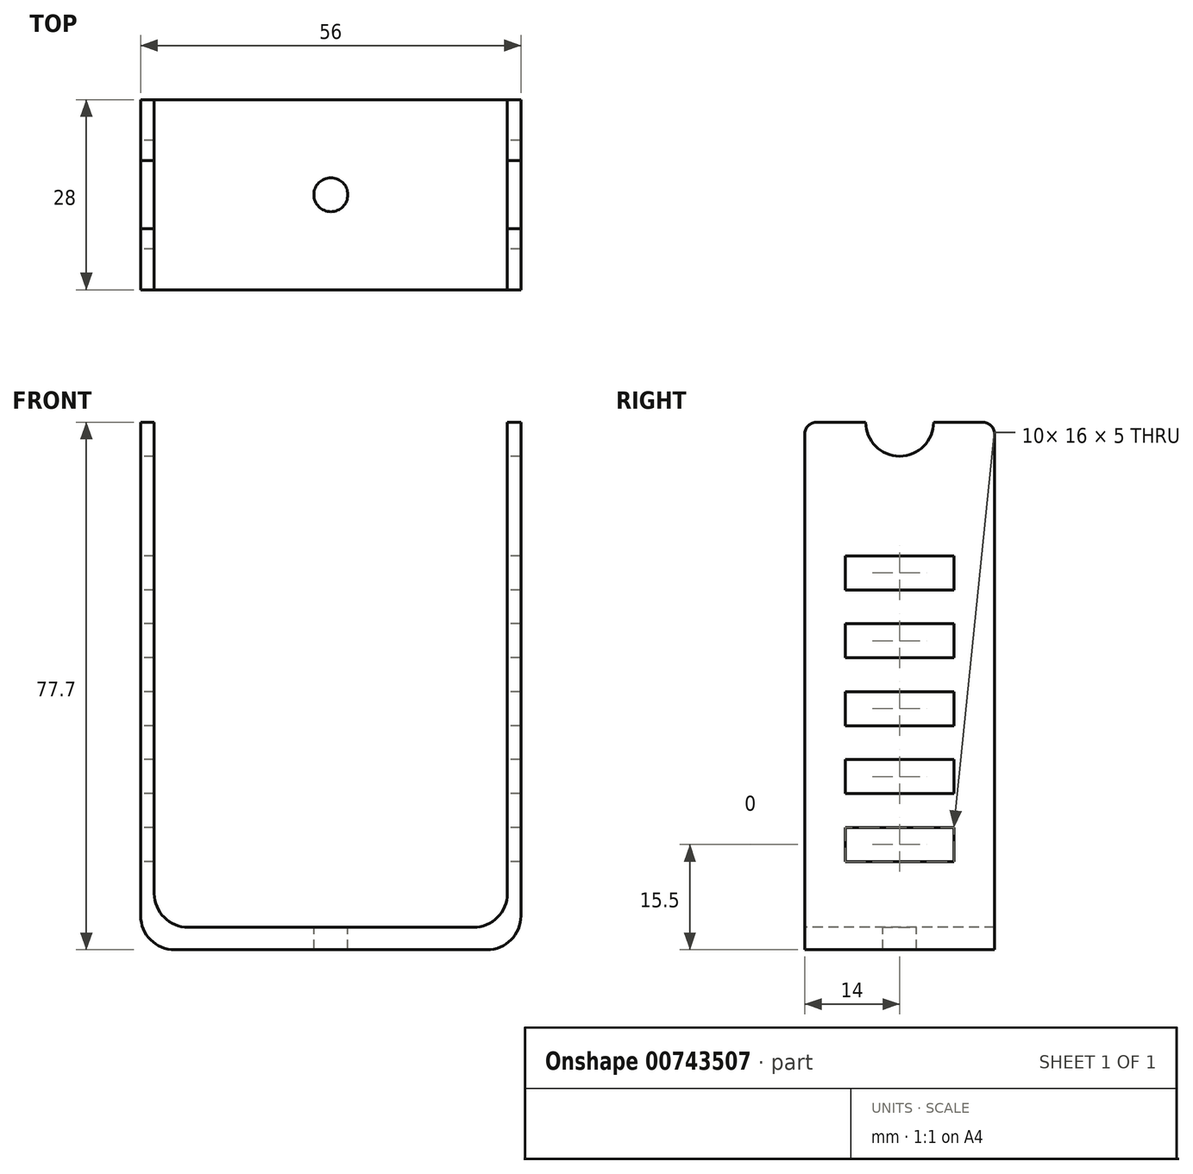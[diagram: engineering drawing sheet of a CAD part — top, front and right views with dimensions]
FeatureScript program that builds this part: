
annotation { "Feature Type Name" : "Feature", "Feature Type Description" : "" }
export const myFeature = defineFeature(function(context is Context, id is Id, definition is map)
    precondition{}
    {
        {
            var Q0;
            Q0=qCreatedBy(makeId("Right.planeOp"),FACE);
            var sketch = newSketch(context, id + "F0", { "sketchPlane" : qUnion([Q0])});
            skLineSegment(sketch, "E0.bottom", {"start": v(-14, 0) * mm, "end": v(14, 0) * mm});
            skLineSegment(sketch, "E0.top", {"start": v(-12.17, 77.7) * mm, "end": v(-5, 77.7) * mm});
            skLineSegment(sketch, "E0.left", {"start": v(-14, 0) * mm, "end": v(-14, 75.87) * mm});
            skLineSegment(sketch, "E0.right", {"start": v(14, 0) * mm, "end": v(14, 75.87) * mm});
            skLineSegment(sketch, "E1.bottom", {"start": v(-8, 18) * mm, "end": v(8, 18) * mm});
            skLineSegment(sketch, "E1.top", {"start": v(-8, 13) * mm, "end": v(8, 13) * mm});
            skLineSegment(sketch, "E1.left", {"start": v(-8, 18) * mm, "end": v(-8, 13) * mm});
            skLineSegment(sketch, "E1.right", {"start": v(8, 18) * mm, "end": v(8, 13) * mm});
            skLineSegment(sketch, "E2.0.1.0", {"start": v(-8, 23) * mm, "end": v(8, 23) * mm});
            skLineSegment(sketch, "E2.0.1.1", {"start": v(8, 28) * mm, "end": v(8, 23) * mm});
            skLineSegment(sketch, "E2.0.1.2", {"start": v(-8, 28) * mm, "end": v(8, 28) * mm});
            skLineSegment(sketch, "E2.0.1.3", {"start": v(-8, 28) * mm, "end": v(-8, 23) * mm});
            skLineSegment(sketch, "E2.0.2.0", {"start": v(-8, 33) * mm, "end": v(8, 33) * mm});
            skLineSegment(sketch, "E2.0.2.1", {"start": v(8, 38) * mm, "end": v(8, 33) * mm});
            skLineSegment(sketch, "E2.0.2.2", {"start": v(-8, 38) * mm, "end": v(8, 38) * mm});
            skLineSegment(sketch, "E2.0.2.3", {"start": v(-8, 38) * mm, "end": v(-8, 33) * mm});
            skLineSegment(sketch, "E2.0.3.0", {"start": v(-8, 43) * mm, "end": v(8, 43) * mm});
            skLineSegment(sketch, "E2.0.3.1", {"start": v(8, 48) * mm, "end": v(8, 43) * mm});
            skLineSegment(sketch, "E2.0.3.2", {"start": v(-8, 48) * mm, "end": v(8, 48) * mm});
            skLineSegment(sketch, "E2.0.3.3", {"start": v(-8, 48) * mm, "end": v(-8, 43) * mm});
            skLineSegment(sketch, "E2.0.4.0", {"start": v(-8, 53) * mm, "end": v(8, 53) * mm});
            skLineSegment(sketch, "E2.0.4.1", {"start": v(8, 58) * mm, "end": v(8, 53) * mm});
            skLineSegment(sketch, "E2.0.4.2", {"start": v(-8, 58) * mm, "end": v(8, 58) * mm});
            skLineSegment(sketch, "E2.0.4.3", {"start": v(-8, 58) * mm, "end": v(-8, 53) * mm});
            skLineSegment(sketch, "E2.direction1", {"start": v(-8, 13) * mm, "end": v(17, 13) * mm, "construction": true});
            skLineSegment(sketch, "E2.direction2", {"start": v(-8, 13) * mm, "end": v(-8, 23) * mm, "construction": true});
            skArc(sketch, "E3", {"start": v(-5, 77.7) * mm, "mid": v(0, 72.7) * mm, "end": v(5, 77.7) * mm});
            skLineSegment(sketch, "E4.trimOffspring", {"start": v(5, 77.7) * mm, "end": v(12.17, 77.7) * mm});
            skPoint(sketch, "E5.visualSharp", {"position": v(-14, 77.7) * mm});
            skArc(sketch, "E5.filletArc", {"start": v(-12.17, 77.7) * mm, "mid": v(-13.46, 77.16) * mm, "end": v(-14, 75.87) * mm});
            skPoint(sketch, "E6.visualSharp", {"position": v(14, 77.7) * mm});
            skArc(sketch, "E6.filletArc", {"start": v(14, 75.87) * mm, "mid": v(13.46, 77.16) * mm, "end": v(12.17, 77.7) * mm});
            skSolve(sketch);
        }
        {
            var Q0;
            Q0=makeQuery(id+"F0.imprint","IMPRINT",FACE,{"disambiguationData":[TD([[makeQuery(id+"F0.imprint","IMPRINT",EDGE,{"derivedFrom":sQuery(id+"F0.wireOp",EDGE,"E0.bottom")}),1.0]])]});
            extrude(context, id + "F1", {"entities" : qUnion([Q0]), "endBound" : BoundingType.SYMMETRIC, "depth" : 56 * mm});
        }
        {
            var Q0;
            Q0=makeQuery(id+"F1.opExtrude","SWEPT_FACE",FACE,{"disambiguationData":[OSD([sQuery(id+"F0.wireOp",EDGE,"E0.top")])]});
            var sketch = newSketch(context, id + "F2", { "sketchPlane" : qUnion([Q0])});
            skLineSegment(sketch, "E7.bottom", {"start": v(-26, 25.02) * mm, "end": v(26, 25.02) * mm});
            skLineSegment(sketch, "E7.top", {"start": v(-26, -24.24) * mm, "end": v(26, -24.24) * mm});
            skLineSegment(sketch, "E7.left", {"start": v(-26, 25.02) * mm, "end": v(-26, -24.24) * mm});
            skLineSegment(sketch, "E7.right", {"start": v(26, 25.02) * mm, "end": v(26, -24.24) * mm});
            skSolve(sketch);
        }
        {
            var Q0;
            Q0=qSketchRegion(id+"F2",true);
            extrude(context, id + "F3", {"entities" : qUnion([Q0]), "operationType" : NewBodyOperationType.REMOVE, "oppositeDirection" : true, "depth" : (77.8 - 3.4) * mm});
        }
        {
            var Q0;
            Q0=makeQuery(id+"F1.opExtrude","CAP_EDGE",EDGE,{"disambiguationData":[OSD([sQuery(id+"F0.wireOp",EDGE,"E0.bottom")])],"isStart":true});
            var Q1;
            Q1=makeQuery(id+"F1.opExtrude","CAP_EDGE",EDGE,{"disambiguationData":[OSD([sQuery(id+"F0.wireOp",EDGE,"E0.bottom")])],"isStart":false});
            var Q2;
            Q2=makeQuery(id+"F3.boolean.opBoolean","COPY",EDGE,{"derivedFrom":makeQuery(id+"F3.opExtrude","CAP_EDGE",EDGE,{"disambiguationData":[OSD([sQuery(id+"F2.wireOp",EDGE,"E7.left")])],"isStart":false})});
            var Q3;
            Q3=makeQuery(id+"F3.boolean.opBoolean","COPY",EDGE,{"derivedFrom":makeQuery(id+"F3.opExtrude","CAP_EDGE",EDGE,{"disambiguationData":[OSD([sQuery(id+"F2.wireOp",EDGE,"E7.right")])],"isStart":false})});
            fillet(context, id + "F4", {"entities" : qUnion([Q0, Q1, Q2, Q3]), "radius" : 5 * mm, "tangentPropagation" : true, "allowEdgeOverflow" : false});
        }
        {
            var Q0;
            Q0=makeQuery(id+"F3.boolean.opBoolean","COPY",FACE,{"derivedFrom":makeQuery(id+"F3.opExtrude","CAP_FACE",FACE,{"disambiguationData":[OSD([sQuery(id+"F2.wireOp",EDGE,"E7.bottom"),sQuery(id+"F2.wireOp",EDGE,"E7.top"),sQuery(id+"F2.wireOp",EDGE,"E7.left"),sQuery(id+"F2.wireOp",EDGE,"E7.right")])],"isStart":false})});
            var sketch = newSketch(context, id + "F5", { "sketchPlane" : qUnion([Q0])});
            skCircle(sketch, "E8", {"center": v(0, 0) * mm, "radius": 2.5 * mm});
            skSolve(sketch);
        }
        {
            var Q0;
            Q0=qSketchRegion(id+"F5",true);
            extrude(context, id + "F6", {"entities" : qUnion([Q0]), "operationType" : NewBodyOperationType.REMOVE, "endBound" : BoundingType.THROUGH_ALL, "oppositeDirection" : true, "depth" : 25 * mm});
        }
    });
